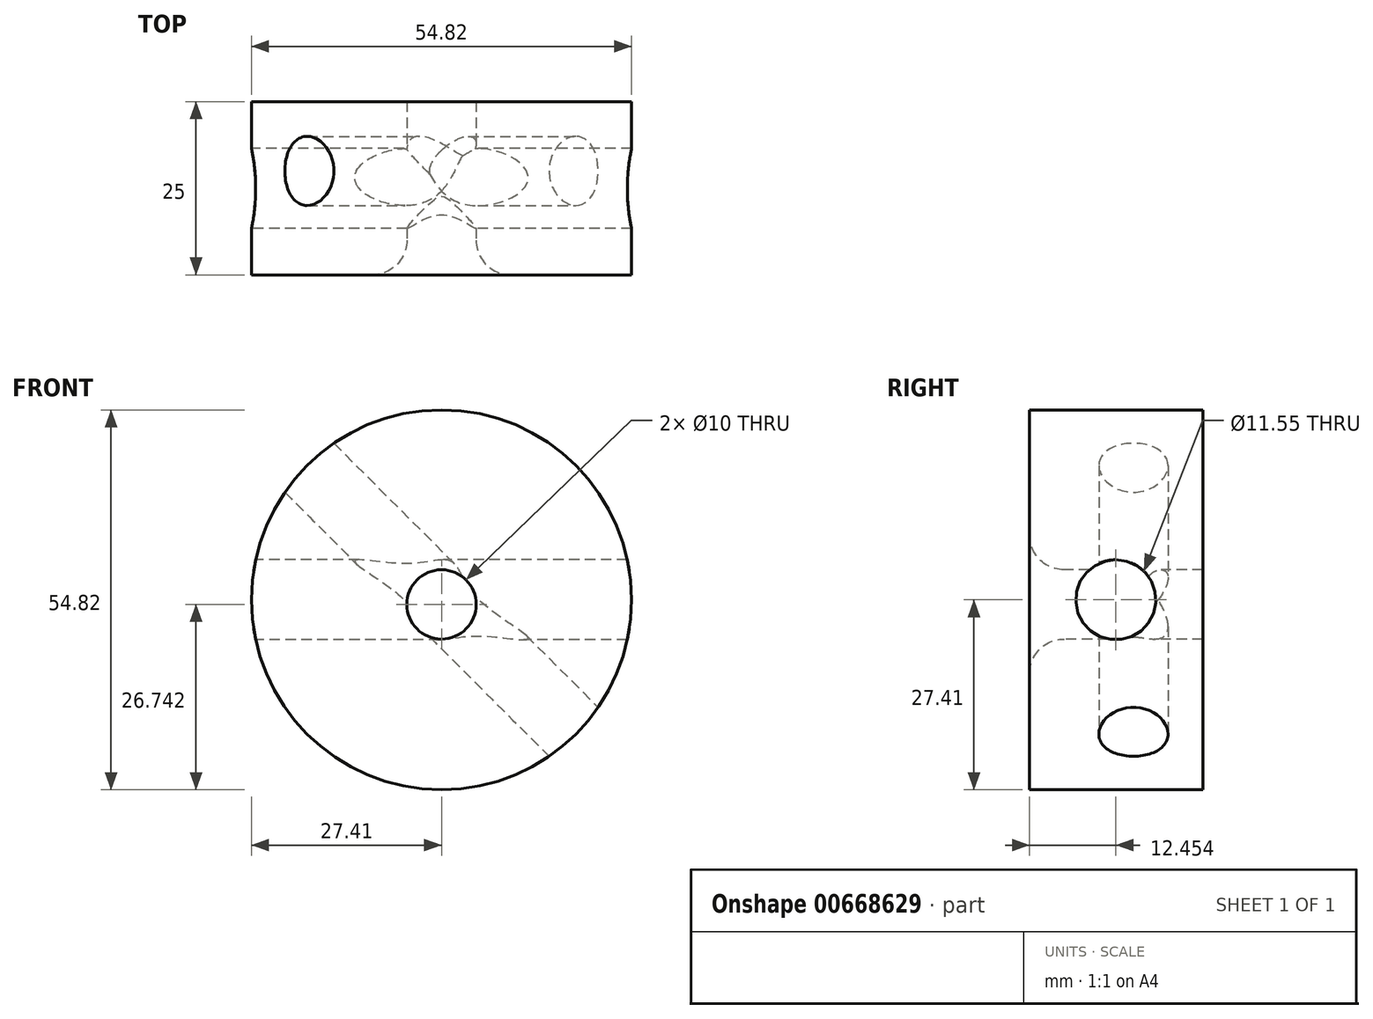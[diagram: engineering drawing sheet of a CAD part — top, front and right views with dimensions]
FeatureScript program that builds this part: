
annotation { "Feature Type Name" : "Feature", "Feature Type Description" : "" }
export const myFeature = defineFeature(function(context is Context, id is Id, definition is map)
    precondition{}
    {
        {
            var Q0;
            Q0=qCreatedBy(makeId("Front.planeOp"),FACE);
            var sketch = newSketch(context, id + "F0", { "sketchPlane" : qUnion([Q0])});
            skCircle(sketch, "E0", {"center": v(0, 0) * mm, "radius": 27.41 * mm});
            skSolve(sketch);
        }
        {
            var Q0;
            Q0=makeQuery(id+"F0.imprint","IMPRINT",FACE,{"disambiguationData":[TD([[makeQuery(id+"F0.imprint","IMPRINT",EDGE,{"derivedFrom":sQuery(id+"F0.wireOp",EDGE,"E0")}),1.0]])]});
            var Q1;
            Q1=sQuery(id+"F0.wireOp",EDGE,"E0");
            extrude(context, id + "F1", {"entities" : qUnion([Q0]), "surfaceEntities" : qUnion([Q1]), "depth" : 25 * mm, "offsetDistance" : 25 * mm});
        }
        {
            var Q0;
            Q0=makeQuery(id+"F1.opExtrude","CAP_FACE",FACE,{"disambiguationData":[OSD([sQuery(id+"F0.wireOp",EDGE,"E0")])],"isStart":false});
            var sketch = newSketch(context, id + "F2", { "sketchPlane" : qUnion([Q0])});
            skCircle(sketch, "E1", {"center": v(0, -0.67) * mm, "radius": 5 * mm});
            skSolve(sketch);
        }
        {
            var Q0;
            Q0=makeQuery(id+"F2.imprint","IMPRINT",FACE,{"disambiguationData":[TD([[makeQuery(id+"F2.imprint","IMPRINT",EDGE,{"derivedFrom":sQuery(id+"F2.wireOp",EDGE,"E1")}),1.0]])]});
            extrude(context, id + "F3", {"entities" : qUnion([Q0]), "operationType" : NewBodyOperationType.REMOVE, "oppositeDirection" : true, "depth" : 25 * mm, "offsetDistance" : 25 * mm, "hasSecondDirection" : true, "secondDirectionOppositeDirection" : false, "secondDirectionDepth" : 25 * mm});
        }
        {
            var Q0;
            Q0=makeQuery(id+"F3.boolean.opBoolean","INTERSECT",EDGE,{"derivedFrom":[makeQuery(id+"F1.opExtrude","CAP_FACE",FACE,{"disambiguationData":[OSD([sQuery(id+"F0.wireOp",EDGE,"E0")])],"isStart":false}),makeQuery(id+"F3.opExtrude","SWEPT_FACE",FACE,{"disambiguationData":[OSD([sQuery(id+"F2.wireOp",EDGE,"E1")])]})]});
            fillet(context, id + "F4", {"entities" : qUnion([Q0]), "radius" : 5 * mm, "tangentPropagation" : true, "allowEdgeOverflow" : false});
        }
        {
            var Q0;
            Q0=qCreatedBy(makeId("Right.planeOp"),FACE);
            var sketch = newSketch(context, id + "F5", { "sketchPlane" : qUnion([Q0])});
            skCircle(sketch, "E2", {"center": v(-12.55, 0) * mm, "radius": 5.78 * mm});
            skSolve(sketch);
        }
        {
            var Q0;
            Q0 = qSketchRegion(id + "F5", true);
            extrude(context, id + "F6", {"entities" : qUnion([Q0]), "operationType" : NewBodyOperationType.REMOVE, "endBound" : BoundingType.THROUGH_ALL, "depth" : 25 * mm, "offsetDistance" : 25 * mm, "hasSecondDirection" : true, "secondDirectionBound" : SecondDirectionBoundingType.THROUGH_ALL, "secondDirectionOppositeDirection" : true, "secondDirectionDepth" : 25 * mm});
        }
        {
            var Q0;
            Q0=qCreatedBy(makeId("Front.planeOp"),FACE);
            var sketch = newSketch(context, id + "F7", { "sketchPlane" : qUnion([Q0])});
            skLineSegment(sketch, "E3", {"start": v(0, 0) * mm, "end": v(-29.3, -29.3) * mm});
            skSolve(sketch);
        }
        {
            var Q0;
            Q0=qCreatedBy(makeId("Top.planeOp"),FACE);
            var Q1;
            Q1=sQuery(id+"F7.wireOp",EDGE,"E3");
            cPlane(context, id + "F8", {"entities" : qUnion([Q0, Q1]), "cplaneType" : CPlaneType.LINE_ANGLE, "offset" : 25 * mm, "angle" : 0 * degree, "width" : 150 * mm, "height" : 150 * mm});
        }
        {
            var Q0;
            Q0=qCreatedBy(id+"F8.planeOp",FACE);
            var sketch = newSketch(context, id + "F9", { "sketchPlane" : qUnion([Q0])});
            skLineSegment(sketch, "E4", {"start": v(0, 0) * mm, "end": v(-54.78, 0) * mm, "construction": true});
            skCircle(sketch, "E5", {"center": v(-10, 0) * mm, "radius": 5 * mm});
            skSolve(sketch);
        }
        {
            var Q0;
            Q0 = qSketchRegion(id + "F9", true);
            extrude(context, id + "F10", {"entities" : qUnion([Q0]), "operationType" : NewBodyOperationType.REMOVE, "endBound" : BoundingType.THROUGH_ALL, "oppositeDirection" : true, "depth" : 25 * mm, "offsetDistance" : 25 * mm, "hasSecondDirection" : true, "secondDirectionBound" : SecondDirectionBoundingType.THROUGH_ALL, "secondDirectionOppositeDirection" : false, "secondDirectionDepth" : 25 * mm});
        }
    });
